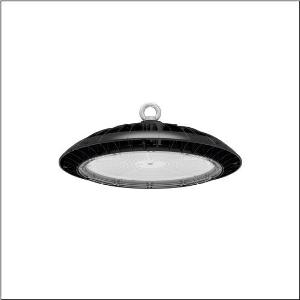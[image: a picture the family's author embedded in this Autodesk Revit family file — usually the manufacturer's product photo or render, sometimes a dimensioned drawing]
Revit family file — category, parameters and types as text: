
# Revit family: highbay_42-l_51hp32mb4mma
name_source: partatom
category: Lighting Fixtures
units: mm (PartAtom-declared; Revit-internal decimal feet)

## family parameters
Cut with Voids When Loaded = No
Host = Face
Light Source = No
Part Type = Normal
Room Calculation Point = No
Round Connector Dimension = Use Diameter
Shared = No

## types (1)
- --- (1 x LED, 28000 lm, 175 W, 4000K)
    Apparent Load = 175 VA
    CIE Flux Codes = 49 82 98 100 100
    Color Rendering = 80
    Color Temperature = 4000K
    Default Elevation = 1800 mm
    Description = Highbay 42-L, high bay luminaire, primary light control with lens, of PC, primary optical cover: cover panel, of PC, transparent, light emission: direct distribution, primary light characteristic: rotationally symmetric, installation type: suspended mounting, surface-mounted, LED, rated luminous flux: 28.000lm, luminous efficacy: 160lm/W, light colour: 840, colour temperature: 4000K, control gear: ON/OFF Multilumen, with cable, 3x 1.0mm², free wire ends, mains connection: 230V, AC, 50Hz, cable length: 1,5m, rated input power: 175W, housing, rotationally symmetric, of diecast aluminium, black, with hook on luminaire side, diameter: 305mm, height: 117mm, protection rating (complete): IP65, insulation class (complete): insulation class I (protective earthing), certification: CE, UKCA, protection symbol: D, impact resistance: IK08, permissible operating ambient temperature: -20..+40°C, corresponds to IFS (International Featured Standards) requirements for safety and quality in the food industry, packaging unit: 1 piece
    Height = 117 mm
    Lamp = 1 x LED
    Lamp Light Flux = 28000 lm
    Lamp Power = 175 W
    Lamp count = 1
    Length = 305 mm
    Luminous efficacy = 160 lm/W
    Manufacturer = Siteco
    ModVariant = No
    Model = 51HP32MB4MMA
    Mounting Place = Ceiling
    Mounting Type = Pendant
    Number of Poles = 1
    OnlyDefault = Yes
    Power Factor = 1
    Product Name = Highbay 42-L
    Product group = high bay luminaire
    ProductGroupID = 902
    Protection Class = Protection class I
    Protection Degree = IP 65
    RLX_Detail_Level = 1
    RLX_Emergency_Light_Flux = 0 lm
    RLX_Emergency_Type = 0
    RLX_Emergency_Type_DB = No
    RlxData = <blob elided: 286485 chars, md5=99fa79bf>
    Socket = socket
    Standby Power = 0 W
    System Light Flux = 28000 lm
    System Power = 175 W
    Type Comments = factory setting: luminous flux: 100 % | (OFF | OFF | OFF)
    Type Image = l_1003932.jpg
    URL = http://relux.com
    VarID = @adj_196521
    Voltage = 0 V
    Weight = 0.00 kg
    Width = 0 mm  [stored 0 ft]

note: [stored X ft] marks values corroborated as IEEE doubles in the binary element streams (Revit-internal decimal feet)

## geometry (parser evidence)
native form markers: Blend x4, Sweep x11
no freeform markers — native parametric forms only
